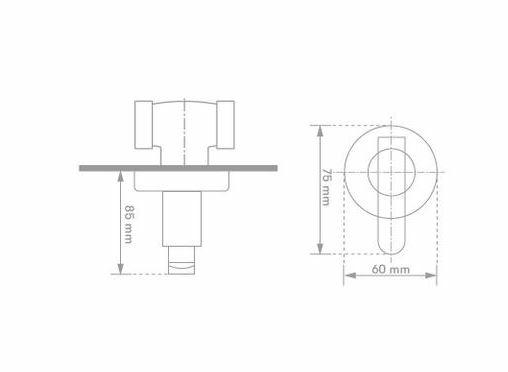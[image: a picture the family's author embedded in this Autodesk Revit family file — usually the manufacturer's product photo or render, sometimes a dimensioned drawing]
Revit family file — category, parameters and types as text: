
# Revit family: 01-2826-11-MEZCLADOR PARED PRISTINA
name_source: partatom
category: Aparatos sanitarios
revit_build: Autodesk Revit 2018 (Build: 20170223_1515(x64)
units: mm (PartAtom-declared; Revit-internal decimal feet)

## family parameters
Anfitrión = Cara
Compartido = No
Corte con vacíos al cargar = No
Cota de conector redondo = Diámetro de uso
Número OmniClass = 23.31.11.00
Punto de cálculo de habitación = No
Tipo de pieza = Normal

## types (1)
- 01-2826-11
    Alto = 60 mm  [stored 0.19685 ft]
    Ancho = 70 mm
    Conexión AC = Sí
    Conexión AF = Sí
    Conexión de residuos = No
    Conexión de ventilación = No
    Descripción = Mezclador Lavamanos
    Distancia entre griferias = 203 mm
    Elevación por defecto = 0 mm  [stored 0 ft]
    Fabricante = Gricol
    Imagen de tipo = <Ninguno>
    Link Ficha Tecnica = http://infotecnica.gricol.com
    Metal Laton Cromado = Metal Laton Cromado
    Metal Zamak Cromado = Metal Zamak Cromado
    Modelo = 01-2826-11
    Plastico ABS Cromado = Plastico ABS Cromado
    Product Name = MEZCLADOR LAVAMANOS PARED PRISTINA
    Profundidad = 85 mm  [stored 0.278871 ft]
    URL = https://www.gricol.com

note: [stored X ft] marks values corroborated as IEEE doubles in the binary element streams (Revit-internal decimal feet)

## geometry (parser evidence)
native form markers: Blend x2, Sweep x14
no freeform markers — native parametric forms only
